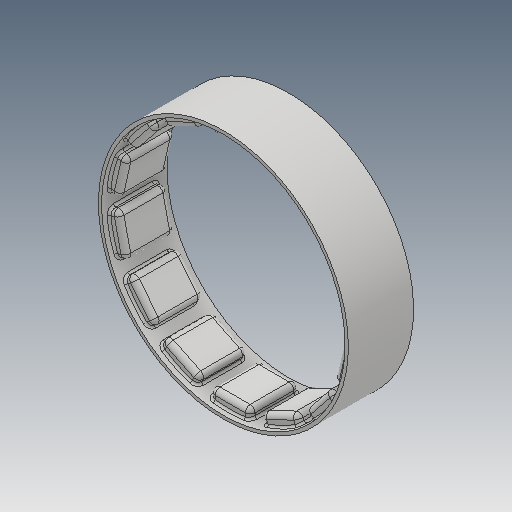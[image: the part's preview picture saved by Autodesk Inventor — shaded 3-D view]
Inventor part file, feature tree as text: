
AUTODESK INVENTOR PART (.ipt)
format: ipt  version: 2018 (Build 220112000, 112)  size: 727,552 bytes
history: native  units: mm
features: fillet x1
ambient origin geometry x8: Origin, YZ Plane, XZ Plane, XY Plane, X Axis, Y Axis, Z Axis, Center Point
bodies: Volumenkörper1 (feature_tree)
feature tree (1):
  fillet  "Fillet2"  [1 undecoded]
note: 1 required parameter value undecoded (feature->parameter linkage not recoverable at this tier; creation-order binding heuristic only, values carry confidence <= 0.55)
